# Revit family: Kinetic High Flow Enclosure LH
name_source: partatom
category: Mechanical Equipment
units: mm (PartAtom-declared; Revit-internal decimal feet)

## family parameters
Always vertical = Yes
Cut with Voids When Loaded = No
OmniClass Number = 23.75.00.00
OmniClass Title = Climate Control (HVAC)
Part Type = Normal
Room Calculation Point = No
Round Connector Dimension = Use Diameter
Shared = No
Work Plane-Based = No

## types (1)
- Kinetic High Flow LH
    22mm or 32mm Condensate Conection = Yes
    AC Frequency Input = 50 Hz nominal
    AC Voltage Input = 220-240 V AC (single phase)
    Country of Manufacture = UK
    Default Elevation = 0 mm  [stored 0 ft]
    Depth = 550mm
    Description = Kinetic Plus E Left Handed
    Filter Options = E3, F3, F5
    Frost Protection = Yes
    Height = 630mm
    IP Rating = IP22
IP22
IP22
    Manufacturer = Vent-Axia
    Model = 449059
    Motor Rating = 150 W (max)
    Operating Humidity = 0% to 95% RH
    Operating Temperature = (-20C to +45C)
(-20C to +45C)
(-20C to +45C)
    Operational and Maintenance Manual = http://www.vent-axia.com
    Product Fuse = 2 A (located on main PCB)
    Rated Power = 190 W (max.)
    Spigot Size = 150mmØ
    Summer Bypass = No
    Supply Fuse = 3 A (located in fused spur)
    URL = www.vent-axia.com
    Warrenty Period = Unit 2 years - Motor 5 years
    Weight = 24 kg
    Width = 775mm

note: [stored X ft] marks values corroborated as IEEE doubles in the binary element streams (Revit-internal decimal feet)

## geometry (parser evidence)
native form markers: Blend x2, Sweep x3
no freeform markers — native parametric forms only
